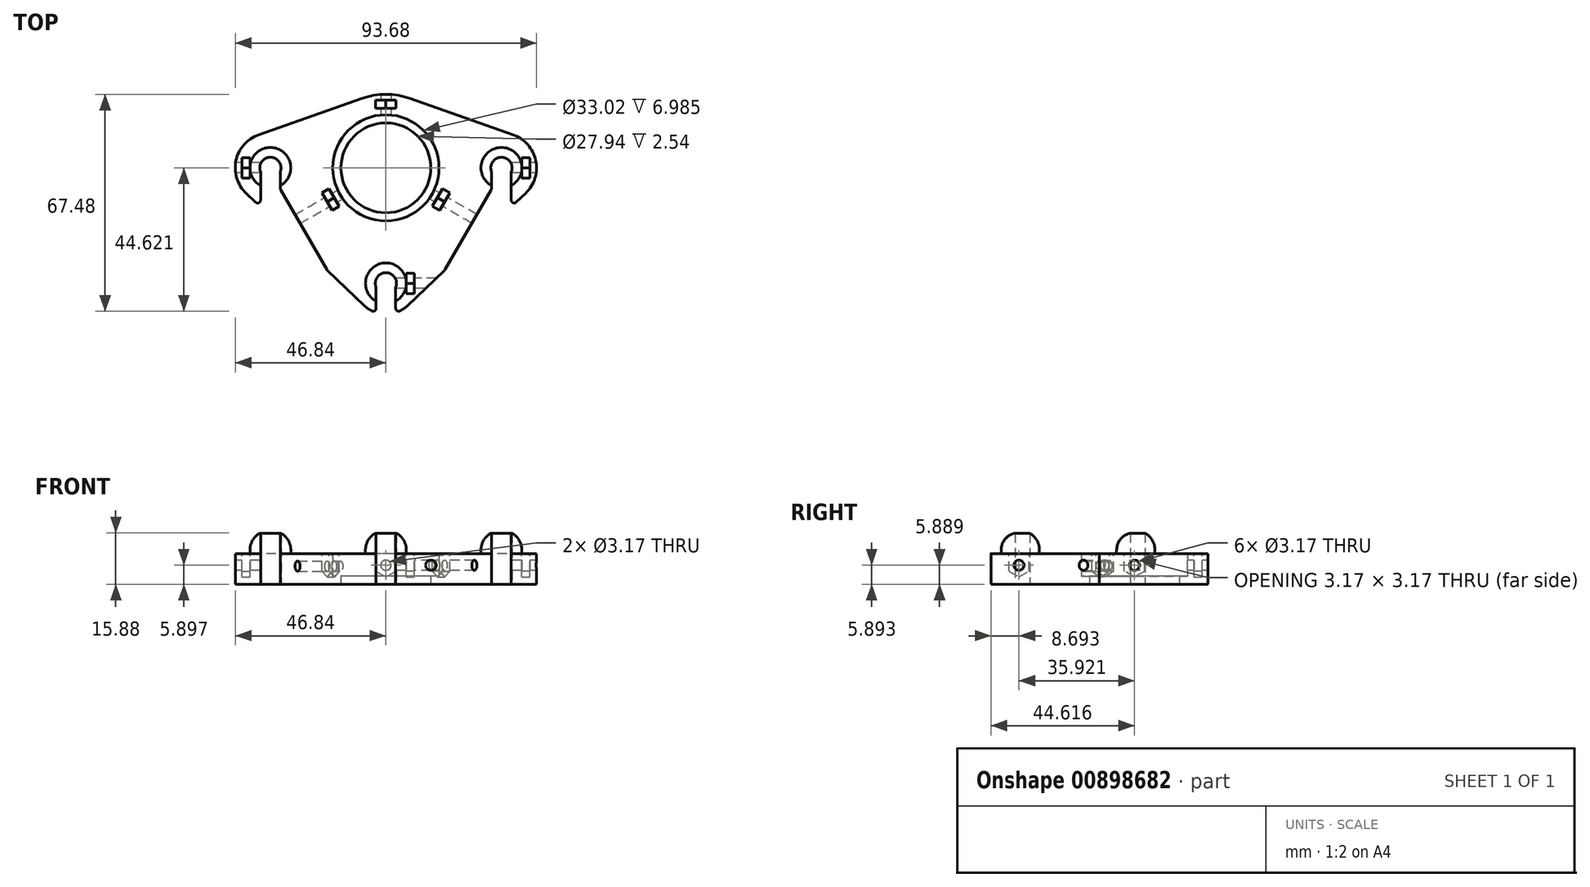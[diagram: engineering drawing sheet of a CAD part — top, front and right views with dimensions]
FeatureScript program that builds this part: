
annotation { "Feature Type Name" : "Feature", "Feature Type Description" : "" }
export const myFeature = defineFeature(function(context is Context, id is Id, definition is map)
    precondition{}
    {
        {
            var Q0;
            Q0=qCreatedBy(makeId("Top.planeOp"),FACE);
            var sketch = newSketch(context, id + "F0", { "sketchPlane" : qUnion([Q0])});
            skArc(sketch, "E0", {"start": v(3.05, -1.27) * mm, "mid": v(0, 3.3) * mm, "end": v(-3.05, -1.27) * mm});
            skArc(sketch, "E1", {"start": v(-32.87, 34.65) * mm, "mid": v(-35.92, 39.22) * mm, "end": v(-38.97, 34.65) * mm});
            skArc(sketch, "E2", {"start": v(38.97, 34.65) * mm, "mid": v(35.92, 39.22) * mm, "end": v(32.87, 34.65) * mm});
            skCircle(sketch, "E3", {"center": v(0, 35.92) * mm, "radius": 16.51 * mm});
            skArc(sketch, "E4.0", {"start": v(-39.55, 46.22) * mm, "mid": v(-46.6, 38.2) * mm, "end": v(-43.45, 28) * mm});
            skArc(sketch, "E5.0", {"start": v(7.6, 57.48) * mm, "mid": v(0, 58.78) * mm, "end": v(-7.6, 57.48) * mm});
            skArc(sketch, "E6.0", {"start": v(43.45, 28) * mm, "mid": v(46.6, 38.2) * mm, "end": v(39.55, 46.22) * mm});
            skArc(sketch, "E7.0", {"start": v(-6.65, -7) * mm, "mid": v(-5.57, -7.88) * mm, "end": v(-4.38, -8.6) * mm});
            skLineSegment(sketch, "E8", {"start": v(-39.55, 46.22) * mm, "end": v(-7.6, 57.48) * mm});
            skLineSegment(sketch, "E9", {"start": v(7.6, 57.48) * mm, "end": v(39.55, 46.22) * mm});
            skLineSegment(sketch, "E10", {"start": v(43.45, 28) * mm, "end": v(40.52, 25.22) * mm});
            skLineSegment(sketch, "E11", {"start": v(-6.65, -7) * mm, "end": v(-18.1, 3.9) * mm});
            skCircle(sketch, "E12", {"center": v(-35.92, 35.92) * mm, "radius": 3.05 * mm, "construction": true});
            skCircle(sketch, "E13", {"center": v(35.92, 35.92) * mm, "radius": 3.05 * mm, "construction": true});
            skCircle(sketch, "E14", {"center": v(0, 0) * mm, "radius": 3.05 * mm, "construction": true});
            skLineSegment(sketch, "E15", {"start": v(-32.87, 35.92) * mm, "end": v(-32.87, 29.77) * mm});
            skLineSegment(sketch, "E16", {"start": v(-38.97, 35.92) * mm, "end": v(-38.97, 25.88) * mm});
            skLineSegment(sketch, "E17", {"start": v(-3.05, 0) * mm, "end": v(-3.05, -7.79) * mm});
            skLineSegment(sketch, "E18", {"start": v(3.05, 0) * mm, "end": v(3.05, -7.79) * mm});
            skPoint(sketch, "E19", {"position": v(-3.05, -1.27) * mm});
            skPoint(sketch, "E20", {"position": v(3.05, -1.27) * mm});
            skArc(sketch, "E21.trimOffspring", {"start": v(4.38, -8.6) * mm, "mid": v(5.57, -7.88) * mm, "end": v(6.65, -7) * mm});
            skLineSegment(sketch, "E22.trimOffspring", {"start": v(-40.52, 25.22) * mm, "end": v(-43.45, 28) * mm});
            skPoint(sketch, "E23.visualSharp", {"position": v(-38.97, 23.75) * mm});
            skArc(sketch, "E23.filletArc", {"start": v(-40.52, 25.22) * mm, "mid": v(-39.52, 25.04) * mm, "end": v(-38.97, 25.88) * mm});
            skPoint(sketch, "E24.visualSharp", {"position": v(-3.05, -9.16) * mm});
            skArc(sketch, "E24.filletArc", {"start": v(-4.38, -8.6) * mm, "mid": v(-3.49, -8.57) * mm, "end": v(-3.05, -7.79) * mm});
            skPoint(sketch, "E25.visualSharp", {"position": v(3.05, -9.16) * mm});
            skArc(sketch, "E25.filletArc", {"start": v(3.05, -7.79) * mm, "mid": v(3.49, -8.57) * mm, "end": v(4.38, -8.6) * mm});
            skLineSegment(sketch, "E26", {"start": v(32.87, 35.92) * mm, "end": v(32.87, 29.77) * mm});
            skLineSegment(sketch, "E27", {"start": v(38.97, 35.92) * mm, "end": v(38.97, 25.88) * mm});
            skLineSegment(sketch, "E28.trimOffspring", {"start": v(18.1, 3.9) * mm, "end": v(6.65, -7) * mm});
            skPoint(sketch, "E29.visualSharp", {"position": v(38.97, 23.75) * mm});
            skCircle(sketch, "E30.0", {"center": v(0, 35.92) * mm, "radius": 13.97 * mm});
            skLineSegment(sketch, "E31", {"start": v(0, 35.92) * mm, "end": v(0, 52.43) * mm, "construction": true});
            skLineSegment(sketch, "E32", {"start": v(0, 35.92) * mm, "end": v(35.3, 15.54) * mm, "construction": true});
            skLineSegment(sketch, "E33", {"start": v(0, 35.92) * mm, "end": v(-35.36, 15.5) * mm, "construction": true});
            skArc(sketch, "E34.filletArc", {"start": v(38.97, 25.88) * mm, "mid": v(39.52, 25.04) * mm, "end": v(40.52, 25.22) * mm});
            skCircle(sketch, "E35.cCircle", {"center": v(0, 35.92) * mm, "radius": 16.51 * mm, "construction": true});
            skLineSegment(sketch, "E35.0", {"start": v(9.53, 52.43) * mm, "end": v(19.06, 35.92) * mm, "construction": true});
            skLineSegment(sketch, "E35.1", {"start": v(19.06, 35.92) * mm, "end": v(9.53, 19.41) * mm, "construction": true});
            skLineSegment(sketch, "E35.2", {"start": v(9.53, 19.41) * mm, "end": v(-9.53, 19.41) * mm, "construction": true});
            skLineSegment(sketch, "E35.3", {"start": v(-9.53, 19.41) * mm, "end": v(-19.06, 35.92) * mm, "construction": true});
            skLineSegment(sketch, "E35.4", {"start": v(-19.06, 35.92) * mm, "end": v(-9.53, 52.43) * mm, "construction": true});
            skLineSegment(sketch, "E35.5", {"start": v(-9.53, 52.43) * mm, "end": v(9.53, 52.43) * mm, "construction": true});
            skPoint(sketch, "E35.0.midPoint", {"position": v(14.3, 44.18) * mm});
            skLineSegment(sketch, "E36", {"start": v(-35.92, 35.92) * mm, "end": v(35.92, 35.92) * mm, "construction": true});
            skCircle(sketch, "E37.0", {"center": v(0, 35.92) * mm, "radius": 31.75 * mm, "construction": true});
            skLineSegment(sketch, "E38", {"start": v(-32.67, 29) * mm, "end": v(-18.37, 4.24) * mm});
            skLineSegment(sketch, "E39", {"start": v(32.67, 29) * mm, "end": v(18.37, 4.24) * mm});
            skPoint(sketch, "E40.visualSharp", {"position": v(-32.87, 29.36) * mm});
            skArc(sketch, "E40.filletArc", {"start": v(-32.87, 29.77) * mm, "mid": v(-32.82, 29.37) * mm, "end": v(-32.67, 29) * mm});
            skPoint(sketch, "E41.visualSharp", {"position": v(-18.26, 4.05) * mm});
            skArc(sketch, "E41.filletArc", {"start": v(-18.37, 4.24) * mm, "mid": v(-18.25, 4.06) * mm, "end": v(-18.1, 3.9) * mm});
            skPoint(sketch, "E42.visualSharp", {"position": v(18.26, 4.05) * mm});
            skArc(sketch, "E42.filletArc", {"start": v(18.1, 3.9) * mm, "mid": v(18.25, 4.06) * mm, "end": v(18.37, 4.24) * mm});
            skPoint(sketch, "E43.visualSharp", {"position": v(32.87, 29.36) * mm});
            skArc(sketch, "E43.filletArc", {"start": v(32.67, 29) * mm, "mid": v(32.82, 29.37) * mm, "end": v(32.87, 29.77) * mm});
            skSolve(sketch);
        }
        {
            var Q0;
            {var subQ5=sQuery(id+"F0.wireOp",EDGE,"E0");Q0=makeQuery(id+"F0.imprint","IMPRINT",FACE,{"disambiguationData":[TD([[makeQuery(id+"F0.imprint","IMPRINT",EDGE,{"derivedFrom":subQ5}),-1.0]])]});}
            extrude(context, id + "F1", {"entities" : qUnion([Q0]), "depth" : 9.52 * mm, "offsetDistance" : 25.4 * mm});
        }
        {
            var Q0;
            Q0=makeQuery(id+"F0.imprint","IMPRINT",FACE,{"disambiguationData":[TD([[makeQuery(id+"F0.imprint","IMPRINT",EDGE,{"derivedFrom":sQuery(id+"F0.wireOp",EDGE,"E3")}),1.0]])]});
            extrude(context, id + "F2", {"entities" : qUnion([Q0]), "operationType" : NewBodyOperationType.ADD, "depth" : 2.54 * mm, "hasOffset" : true, "offsetDistance" : 6.35 * mm});
        }
        {
            var Q0;
            Q0=makeQuery(id+"F1.opExtrude","CAP_FACE",FACE,{"disambiguationData":[OSD([sQuery(id+"F0.wireOp",EDGE,"E0"),sQuery(id+"F0.wireOp",EDGE,"E1"),sQuery(id+"F0.wireOp",EDGE,"E2"),sQuery(id+"F0.wireOp",EDGE,"E3"),sQuery(id+"F0.wireOp",EDGE,"E4.0"),sQuery(id+"F0.wireOp",EDGE,"E5.0"),sQuery(id+"F0.wireOp",EDGE,"E6.0"),sQuery(id+"F0.wireOp",EDGE,"E7.0"),sQuery(id+"F0.wireOp",EDGE,"E8"),sQuery(id+"F0.wireOp",EDGE,"E9"),sQuery(id+"F0.wireOp",EDGE,"E10"),sQuery(id+"F0.wireOp",EDGE,"E11"),sQuery(id+"F0.wireOp",EDGE,"E15"),sQuery(id+"F0.wireOp",EDGE,"E16"),sQuery(id+"F0.wireOp",EDGE,"E17"),sQuery(id+"F0.wireOp",EDGE,"E18"),sQuery(id+"F0.wireOp",EDGE,"E21.trimOffspring"),sQuery(id+"F0.wireOp",EDGE,"E22.trimOffspring"),sQuery(id+"F0.wireOp",EDGE,"E23.filletArc"),sQuery(id+"F0.wireOp",EDGE,"E24.filletArc"),sQuery(id+"F0.wireOp",EDGE,"E25.filletArc"),sQuery(id+"F0.wireOp",EDGE,"E26"),sQuery(id+"F0.wireOp",EDGE,"E27"),sQuery(id+"F0.wireOp",EDGE,"E28.trimOffspring"),sQuery(id+"F0.wireOp",EDGE,"3LgmcLzA-5pnU-fFz7-q1u9-bpeBtAsCO3An"),sQuery(id+"F0.wireOp",EDGE,"4eo9xTR6-c1Fu-en91-zOid-S4E7wj55DmDX"),sQuery(id+"F0.wireOp",EDGE,"E34.filletArc"),sQuery(id+"F0.wireOp",EDGE,"0de4be46-af92-408f-a28e-b5eb566cc358.filletArc"),sQuery(id+"F0.wireOp",EDGE,"cd97e584-8722-4711-bad1-4d169eb79cda.filletArc"),sQuery(id+"F0.wireOp",EDGE,"a80f9f6f-3806-41d0-9fd0-596e0330244b.filletArc"),sQuery(id+"F0.wireOp",EDGE,"743a1c7c-530f-41f0-bede-06812bb20fe3.filletArc")])],"isStart":false});
            var sketch = newSketch(context, id + "F3", { "sketchPlane" : qUnion([Q0])});
            skCircle(sketch, "E44", {"center": v(-35.92, 35.92) * mm, "radius": 6.35 * mm});
            skCircle(sketch, "E45", {"center": v(35.92, 35.92) * mm, "radius": 6.35 * mm});
            skCircle(sketch, "E46", {"center": v(0, 0) * mm, "radius": 6.35 * mm});
            skSolve(sketch);
        }
        {
            var Q0;
            Q0=makeQuery(id+"F1.opExtrude","CAP_FACE",FACE,{"disambiguationData":[OSD([sQuery(id+"F0.wireOp",EDGE,"E0"),sQuery(id+"F0.wireOp",EDGE,"E1"),sQuery(id+"F0.wireOp",EDGE,"E2"),sQuery(id+"F0.wireOp",EDGE,"E3"),sQuery(id+"F0.wireOp",EDGE,"E4.0"),sQuery(id+"F0.wireOp",EDGE,"E5.0"),sQuery(id+"F0.wireOp",EDGE,"E6.0"),sQuery(id+"F0.wireOp",EDGE,"E7.0"),sQuery(id+"F0.wireOp",EDGE,"E8"),sQuery(id+"F0.wireOp",EDGE,"E9"),sQuery(id+"F0.wireOp",EDGE,"E10"),sQuery(id+"F0.wireOp",EDGE,"E11"),sQuery(id+"F0.wireOp",EDGE,"E15"),sQuery(id+"F0.wireOp",EDGE,"E16"),sQuery(id+"F0.wireOp",EDGE,"E17"),sQuery(id+"F0.wireOp",EDGE,"E18"),sQuery(id+"F0.wireOp",EDGE,"E21.trimOffspring"),sQuery(id+"F0.wireOp",EDGE,"E22.trimOffspring"),sQuery(id+"F0.wireOp",EDGE,"E23.filletArc"),sQuery(id+"F0.wireOp",EDGE,"2f08ad09-a47d-42bd-8f0e-b7f58f6490e4.filletArc"),sQuery(id+"F0.wireOp",EDGE,"E24.filletArc"),sQuery(id+"F0.wireOp",EDGE,"E25.filletArc"),sQuery(id+"F0.wireOp",EDGE,"E26"),sQuery(id+"F0.wireOp",EDGE,"E27"),sQuery(id+"F0.wireOp",EDGE,"E28.trimOffspring"),sQuery(id+"F0.wireOp",EDGE,"bfc3d6b4-ed7b-404a-8939-94d15189dd00.filletArc"),sQuery(id+"F0.wireOp",EDGE,"E29.filletArc")])],"isStart":false});
            var sketch = newSketch(context, id + "F4", { "sketchPlane" : qUnion([Q0])});
            skLineSegment(sketch, "E47", {"start": v(-3.18, 54.46) * mm, "end": v(-3.18, 57) * mm});
            skLineSegment(sketch, "E48", {"start": v(-3.18, 57) * mm, "end": v(3.17, 57) * mm});
            skLineSegment(sketch, "E49", {"start": v(3.17, 57) * mm, "end": v(3.17, 54.46) * mm});
            skLineSegment(sketch, "E50", {"start": v(3.17, 54.46) * mm, "end": v(-3.18, 54.46) * mm});
            skLineSegment(sketch, "E51", {"start": v(0, 52.43) * mm, "end": v(0, 54.46) * mm});
            skLineSegment(sketch, "E52.1.0", {"start": v(-17.65, 29.4) * mm, "end": v(-14.47, 23.9) * mm});
            skLineSegment(sketch, "E52.1.1", {"start": v(-19.85, 28.13) * mm, "end": v(-17.65, 29.4) * mm});
            skLineSegment(sketch, "E52.1.2", {"start": v(-16.67, 22.63) * mm, "end": v(-19.85, 28.13) * mm});
            skLineSegment(sketch, "E52.1.3", {"start": v(-14.47, 23.9) * mm, "end": v(-16.67, 22.63) * mm});
            skLineSegment(sketch, "E52.2.0", {"start": v(14.47, 23.9) * mm, "end": v(17.65, 29.4) * mm});
            skLineSegment(sketch, "E52.2.1", {"start": v(16.67, 22.63) * mm, "end": v(14.47, 23.9) * mm});
            skLineSegment(sketch, "E52.2.2", {"start": v(19.85, 28.13) * mm, "end": v(16.67, 22.63) * mm});
            skLineSegment(sketch, "E52.2.3", {"start": v(17.65, 29.4) * mm, "end": v(19.85, 28.13) * mm});
            skPoint(sketch, "E52.center", {"position": v(0, 35.92) * mm});
            skCircle(sketch, "E53", {"center": v(-35.92, 35.92) * mm, "radius": 6.35 * mm});
            skCircle(sketch, "E54", {"center": v(35.92, 35.92) * mm, "radius": 6.35 * mm});
            skCircle(sketch, "E55", {"center": v(0, 0) * mm, "radius": 6.35 * mm});
            skLineSegment(sketch, "E56", {"start": v(-42.27, 39.1) * mm, "end": v(-42.27, 32.75) * mm});
            skLineSegment(sketch, "E57", {"start": v(-42.27, 32.75) * mm, "end": v(-44.81, 32.75) * mm});
            skLineSegment(sketch, "E58", {"start": v(-44.81, 32.75) * mm, "end": v(-44.81, 39.1) * mm});
            skLineSegment(sketch, "E59", {"start": v(-44.81, 39.1) * mm, "end": v(-42.27, 39.1) * mm});
            skLineSegment(sketch, "E60", {"start": v(-35.92, 35.92) * mm, "end": v(-42.27, 35.92) * mm, "construction": true});
            skLineSegment(sketch, "E61", {"start": v(42.27, 32.75) * mm, "end": v(42.27, 39.1) * mm});
            skLineSegment(sketch, "E62", {"start": v(42.27, 39.1) * mm, "end": v(44.81, 39.1) * mm});
            skLineSegment(sketch, "E63", {"start": v(44.81, 39.1) * mm, "end": v(44.81, 32.75) * mm});
            skLineSegment(sketch, "E64", {"start": v(44.81, 32.75) * mm, "end": v(42.27, 32.75) * mm});
            skLineSegment(sketch, "E65", {"start": v(35.92, 35.92) * mm, "end": v(42.27, 35.92) * mm, "construction": true});
            skLineSegment(sketch, "E66", {"start": v(8.9, 3.18) * mm, "end": v(8.9, -3.18) * mm});
            skLineSegment(sketch, "E67", {"start": v(8.9, -3.18) * mm, "end": v(6.35, -3.18) * mm});
            skLineSegment(sketch, "E68", {"start": v(6.35, -3.18) * mm, "end": v(6.35, 3.18) * mm});
            skLineSegment(sketch, "E69", {"start": v(6.35, 3.17) * mm, "end": v(8.9, 3.17) * mm});
            skLineSegment(sketch, "E70", {"start": v(8.9, 0) * mm, "end": v(0, 0) * mm, "construction": true});
            skSolve(sketch);
        }
        {
            var Q0;
            Q0=makeQuery(id+"F4.imprint","IMPRINT",FACE,{"disambiguationData":[TD([[makeQuery(id+"F4.imprint","IMPRINT",EDGE,{"derivedFrom":sQuery(id+"F4.wireOp",EDGE,"E52.2.0")}),-1.0]])]});
            var Q1;
            {var subQ3=sQuery(id+"F4.wireOp",EDGE,"E47");Q1=makeQuery(id+"F4.imprint","IMPRINT",FACE,{"disambiguationData":[TD([[makeQuery(id+"F4.imprint","IMPRINT",EDGE,{"derivedFrom":subQ3}),-1.0]])]});}
            var Q2;
            Q2=makeQuery(id+"F4.imprint","IMPRINT",FACE,{"disambiguationData":[TD([[makeQuery(id+"F4.imprint","IMPRINT",EDGE,{"derivedFrom":sQuery(id+"F4.wireOp",EDGE,"E52.1.0")}),-1.0]])]});
            var Q3;
            {var subQ0=sQuery(id+"F4.wireOp",EDGE,"E57");Q3=makeQuery(id+"F4.imprint","IMPRINT",FACE,{"disambiguationData":[TD([[makeQuery(id+"F4.imprint","IMPRINT",EDGE,{"derivedFrom":subQ0}),-1.0]])]});}
            var Q4;
            {var subQ0=sQuery(id+"F4.wireOp",EDGE,"E62");Q4=makeQuery(id+"F4.imprint","IMPRINT",FACE,{"disambiguationData":[TD([[makeQuery(id+"F4.imprint","IMPRINT",EDGE,{"derivedFrom":subQ0}),-1.0]])]});}
            var Q5;
            Q5=makeQuery(id+"F4.imprint","IMPRINT",FACE,{"disambiguationData":[TD([[makeQuery(id+"F4.imprint","IMPRINT",EDGE,{"derivedFrom":sQuery(id+"F4.wireOp",EDGE,"E66")}),-1.0]])]});
            extrude(context, id + "F5", {"entities" : qUnion([Q0, Q1, Q2, Q3, Q4, Q5]), "operationType" : NewBodyOperationType.REMOVE, "oppositeDirection" : true, "depth" : 8.64 * mm, "offsetDistance" : 25.4 * mm});
        }
        {
            var Q0;
            Q0=makeQuery(id+"F5.boolean.opBoolean","COPY",EDGE,{"derivedFrom":makeQuery(id+"F5.opExtrude","CAP_EDGE",EDGE,{"disambiguationData":[OSD([sQuery(id+"F4.wireOp",EDGE,"E52.1.1")])],"isStart":false})});
            var Q1;
            Q1=makeQuery(id+"F5.boolean.opBoolean","COPY",EDGE,{"derivedFrom":makeQuery(id+"F5.opExtrude","CAP_EDGE",EDGE,{"disambiguationData":[OSD([sQuery(id+"F4.wireOp",EDGE,"E52.1.3")])],"isStart":false})});
            var Q2;
            Q2=makeQuery(id+"F5.boolean.opBoolean","COPY",EDGE,{"derivedFrom":makeQuery(id+"F5.opExtrude","CAP_EDGE",EDGE,{"disambiguationData":[OSD([sQuery(id+"F4.wireOp",EDGE,"E47")])],"isStart":false})});
            var Q3;
            Q3=makeQuery(id+"F5.boolean.opBoolean","COPY",EDGE,{"derivedFrom":makeQuery(id+"F5.opExtrude","CAP_EDGE",EDGE,{"disambiguationData":[OSD([sQuery(id+"F4.wireOp",EDGE,"E49")])],"isStart":false})});
            var Q4;
            Q4=makeQuery(id+"F5.boolean.opBoolean","COPY",EDGE,{"derivedFrom":makeQuery(id+"F5.opExtrude","CAP_EDGE",EDGE,{"disambiguationData":[OSD([sQuery(id+"F4.wireOp",EDGE,"E52.2.3")])],"isStart":false})});
            var Q5;
            Q5=makeQuery(id+"F5.boolean.opBoolean","COPY",EDGE,{"derivedFrom":makeQuery(id+"F5.opExtrude","CAP_EDGE",EDGE,{"disambiguationData":[OSD([sQuery(id+"F4.wireOp",EDGE,"E52.2.1")])],"isStart":false})});
            var Q6;
            Q6=makeQuery(id+"F5.boolean.opBoolean","COPY",EDGE,{"derivedFrom":makeQuery(id+"F5.opExtrude","CAP_EDGE",EDGE,{"disambiguationData":[OSD([sQuery(id+"F4.wireOp",EDGE,"E59")])],"isStart":false})});
            var Q7;
            Q7=makeQuery(id+"F5.boolean.opBoolean","COPY",EDGE,{"derivedFrom":makeQuery(id+"F5.opExtrude","CAP_EDGE",EDGE,{"disambiguationData":[OSD([sQuery(id+"F4.wireOp",EDGE,"E57")])],"isStart":false})});
            var Q8;
            Q8=makeQuery(id+"F5.boolean.opBoolean","COPY",EDGE,{"derivedFrom":makeQuery(id+"F5.opExtrude","CAP_EDGE",EDGE,{"disambiguationData":[OSD([sQuery(id+"F4.wireOp",EDGE,"E69")])],"isStart":false})});
            var Q9;
            Q9=makeQuery(id+"F5.boolean.opBoolean","COPY",EDGE,{"derivedFrom":makeQuery(id+"F5.opExtrude","CAP_EDGE",EDGE,{"disambiguationData":[OSD([sQuery(id+"F4.wireOp",EDGE,"E67")])],"isStart":false})});
            var Q10;
            Q10=makeQuery(id+"F5.boolean.opBoolean","COPY",EDGE,{"derivedFrom":makeQuery(id+"F5.opExtrude","CAP_EDGE",EDGE,{"disambiguationData":[OSD([sQuery(id+"F4.wireOp",EDGE,"E62")])],"isStart":false})});
            var Q11;
            Q11=makeQuery(id+"F5.boolean.opBoolean","COPY",EDGE,{"derivedFrom":makeQuery(id+"F5.opExtrude","CAP_EDGE",EDGE,{"disambiguationData":[OSD([sQuery(id+"F4.wireOp",EDGE,"E64")])],"isStart":false})});
            chamfer(context, id + "F6", {"entities" : qUnion([Q0, Q1, Q2, Q3, Q4, Q5, Q6, Q7, Q8, Q9, Q10, Q11]), "chamferType" : ChamferType.OFFSET_ANGLE, "width" : 3.17 * mm, "oppositeDirection" : false, "angle" : 60 * degree, "tangentPropagation" : true});
        }
        {
            var Q0;
            Q0=makeQuery(id+"F5.boolean.opBoolean","COPY",FACE,{"derivedFrom":makeQuery(id+"F5.opExtrude","SWEPT_FACE",FACE,{"disambiguationData":[OSD([sQuery(id+"F4.wireOp",EDGE,"E48")])]})});
            var sketch = newSketch(context, id + "F7", { "sketchPlane" : qUnion([Q0])});
            skLineSegment(sketch, "E71", {"start": v(3.18, 4.06) * mm, "end": v(0, 2.23) * mm});
            skLineSegment(sketch, "E72", {"start": v(0, 2.23) * mm, "end": v(-3.17, 4.06) * mm});
            skLineSegment(sketch, "E73", {"start": v(-3.17, 4.06) * mm, "end": v(-3.17, 7.73) * mm});
            skLineSegment(sketch, "E74", {"start": v(3.18, 7.73) * mm, "end": v(3.18, 4.06) * mm});
            skLineSegment(sketch, "E75", {"start": v(3.18, 7.73) * mm, "end": v(0, 9.56) * mm});
            skPoint(sketch, "E75.endSnap0", {"position": v(0, 9.53) * mm});
            skLineSegment(sketch, "E76", {"start": v(0, 9.56) * mm, "end": v(-3.17, 7.73) * mm});
            skLineSegment(sketch, "E77", {"start": v(0, 2.23) * mm, "end": v(0, 5.9) * mm, "construction": true});
            skLineSegment(sketch, "E78", {"start": v(0, 5.9) * mm, "end": v(-3.17, 4.06) * mm, "construction": true});
            skLineSegment(sketch, "E79", {"start": v(0, 5.9) * mm, "end": v(3.18, 7.73) * mm, "construction": true});
            skLineSegment(sketch, "E80", {"start": v(0, 5.9) * mm, "end": v(0, 9.56) * mm, "construction": true});
            skCircle(sketch, "E81", {"center": v(0, 5.9) * mm, "radius": 1.59 * mm});
            skSolve(sketch);
        }
        {
            var Q0;
            Q0=makeQuery(id+"F5.boolean.opBoolean","COPY",FACE,{"derivedFrom":makeQuery(id+"F5.opExtrude","SWEPT_FACE",FACE,{"disambiguationData":[OSD([sQuery(id+"F4.wireOp",EDGE,"E52.1.2")])]})});
            var sketch = newSketch(context, id + "F8", { "sketchPlane" : qUnion([Q0])});
            skLineSegment(sketch, "E82", {"start": v(34.2, 3.78) * mm, "end": v(31.03, 1.94) * mm});
            skLineSegment(sketch, "E83", {"start": v(31.03, 1.94) * mm, "end": v(27.86, 3.78) * mm});
            skLineSegment(sketch, "E84", {"start": v(27.86, 3.78) * mm, "end": v(27.86, 7.44) * mm});
            skLineSegment(sketch, "E85", {"start": v(34.2, 7.44) * mm, "end": v(34.2, 3.78) * mm});
            skLineSegment(sketch, "E86", {"start": v(34.2, 7.44) * mm, "end": v(31.03, 9.26) * mm});
            skLineSegment(sketch, "E87", {"start": v(31.03, 9.26) * mm, "end": v(27.86, 7.44) * mm});
            skCircle(sketch, "E88", {"center": v(31.03, 5.6) * mm, "radius": 1.59 * mm});
            skSolve(sketch);
        }
        {
            var Q0;
            Q0=makeQuery(id+"F5.boolean.opBoolean","COPY",FACE,{"derivedFrom":makeQuery(id+"F5.opExtrude","SWEPT_FACE",FACE,{"disambiguationData":[OSD([sQuery(id+"F4.wireOp",EDGE,"E52.2.2")])]})});
            var sketch = newSketch(context, id + "F9", { "sketchPlane" : qUnion([Q0])});
            skLineSegment(sketch, "E89", {"start": v(-27.95, 4.06) * mm, "end": v(-31.12, 2.24) * mm});
            skLineSegment(sketch, "E90", {"start": v(-31.12, 2.24) * mm, "end": v(-34.28, 4.06) * mm});
            skLineSegment(sketch, "E91", {"start": v(-34.28, 4.06) * mm, "end": v(-34.28, 7.72) * mm});
            skLineSegment(sketch, "E92", {"start": v(-27.95, 7.72) * mm, "end": v(-27.95, 4.06) * mm});
            skLineSegment(sketch, "E93", {"start": v(-27.95, 7.72) * mm, "end": v(-31.12, 9.55) * mm});
            skLineSegment(sketch, "E94", {"start": v(-31.12, 9.55) * mm, "end": v(-34.28, 7.72) * mm});
            skCircle(sketch, "E95", {"center": v(-31.12, 5.9) * mm, "radius": 1.59 * mm});
            skLineSegment(sketch, "E96", {"start": v(-31.12, 2.24) * mm, "end": v(-31.12, 5.9) * mm, "construction": true});
            skLineSegment(sketch, "E97", {"start": v(-31.12, 5.9) * mm, "end": v(-34.28, 4.06) * mm, "construction": true});
            skLineSegment(sketch, "E98", {"start": v(-31.12, 9.55) * mm, "end": v(-31.12, 5.9) * mm, "construction": true});
            skLineSegment(sketch, "E99", {"start": v(-27.95, 7.72) * mm, "end": v(-31.12, 5.9) * mm, "construction": true});
            skSolve(sketch);
        }
        {
            var Q0;
            Q0=makeQuery(id+"F7.imprint","IMPRINT",FACE,{"disambiguationData":[TD([[makeQuery(id+"F7.imprint","IMPRINT",EDGE,{"derivedFrom":sQuery(id+"F7.wireOp",EDGE,"E81")}),1.0]])]});
            extrude(context, id + "F10", {"entities" : qUnion([Q0]), "operationType" : NewBodyOperationType.REMOVE, "oppositeDirection" : true, "depth" : 10.16 * mm, "offsetDistance" : 25.4 * mm, "symmetric" : true});
        }
        {
            var Q0;
            Q0=makeQuery(id+"F8.imprint","IMPRINT",FACE,{"disambiguationData":[TD([[makeQuery(id+"F8.imprint","IMPRINT",EDGE,{"derivedFrom":sQuery(id+"F8.wireOp",EDGE,"E88")}),1.0]])]});
            var Q1;
            Q1=sQuery(id+"F8.wireOp",EDGE,"E88");
            extrude(context, id + "F11", {"entities" : qUnion([Q0]), "operationType" : NewBodyOperationType.REMOVE, "surfaceEntities" : qUnion([Q1]), "oppositeDirection" : true, "depth" : 40.64 * mm, "offsetDistance" : 25.4 * mm, "symmetric" : true});
        }
        {
            var Q0;
            Q0=makeQuery(id+"F9.imprint","IMPRINT",FACE,{"disambiguationData":[TD([[makeQuery(id+"F9.imprint","IMPRINT",EDGE,{"derivedFrom":sQuery(id+"F9.wireOp",EDGE,"E95")}),1.0]])]});
            var Q1;
            Q1=sQuery(id+"F9.wireOp",EDGE,"E95");
            extrude(context, id + "F12", {"entities" : qUnion([Q0]), "operationType" : NewBodyOperationType.REMOVE, "surfaceEntities" : qUnion([Q1]), "oppositeDirection" : true, "depth" : 40.64 * mm, "offsetDistance" : 25.4 * mm, "symmetric" : true});
        }
        {
            var Q0;
            {var subQ5=makeQuery(id+"F1.opExtrude","CAP_EDGE",EDGE,{"disambiguationData":[OSD([sQuery(id+"F0.wireOp",EDGE,"E1")])],"isStart":false});Q0=makeQuery(id+"F3.imprint","IMPRINT",FACE,{"disambiguationData":[TD([[makeQuery(id+"F3.imprint","IMPRINT",EDGE,{"derivedFrom":subQ5}),-1.0]])]});}
            var Q1;
            {var subQ5=makeQuery(id+"F1.opExtrude","CAP_EDGE",EDGE,{"disambiguationData":[OSD([sQuery(id+"F0.wireOp",EDGE,"E2")])],"isStart":false});Q1=makeQuery(id+"F3.imprint","IMPRINT",FACE,{"disambiguationData":[TD([[makeQuery(id+"F3.imprint","IMPRINT",EDGE,{"derivedFrom":subQ5}),-1.0]])]});}
            var Q2;
            {var subQ5=makeQuery(id+"F1.opExtrude","CAP_EDGE",EDGE,{"disambiguationData":[OSD([sQuery(id+"F0.wireOp",EDGE,"E0")])],"isStart":false});Q2=makeQuery(id+"F3.imprint","IMPRINT",FACE,{"disambiguationData":[TD([[makeQuery(id+"F3.imprint","IMPRINT",EDGE,{"derivedFrom":subQ5}),-1.0]])]});}
            extrude(context, id + "F13", {"entities" : qUnion([Q0, Q1, Q2]), "operationType" : NewBodyOperationType.ADD, "depth" : 6.35 * mm, "offsetDistance" : 25.4 * mm});
        }
        {
            var Q0;
            Q0=makeQuery(id+"F13.opExtrude","CAP_EDGE",EDGE,{"disambiguationData":[OSD([sQuery(id+"F3.wireOp",EDGE,"E44")])],"isStart":false});
            var Q1;
            Q1=makeQuery(id+"F13.opExtrude","CAP_EDGE",EDGE,{"disambiguationData":[OSD([sQuery(id+"F3.wireOp",EDGE,"E45")])],"isStart":false});
            var Q2;
            Q2=makeQuery(id+"F13.opExtrude","CAP_EDGE",EDGE,{"disambiguationData":[OSD([sQuery(id+"F3.wireOp",EDGE,"E46")])],"isStart":false});
            fillet(context, id + "F14", {"entities" : qUnion([Q0, Q1, Q2]), "radius" : 6.1 * mm, "tangentPropagation" : true, "allowEdgeOverflow" : false});
        }
        {
            var Q0;
            Q0=makeQuery(id+"F5.boolean.opBoolean","COPY",FACE,{"derivedFrom":makeQuery(id+"F5.opExtrude","SWEPT_FACE",FACE,{"disambiguationData":[OSD([sQuery(id+"F4.wireOp",EDGE,"E58")])]})});
            var sketch = newSketch(context, id + "F15", { "sketchPlane" : qUnion([Q0])});
            skLineSegment(sketch, "E100", {"start": v(39.08, 4.06) * mm, "end": v(35.91, 2.24) * mm});
            skLineSegment(sketch, "E101", {"start": v(35.91, 2.24) * mm, "end": v(32.75, 4.06) * mm});
            skLineSegment(sketch, "E102", {"start": v(32.75, 4.06) * mm, "end": v(32.75, 7.72) * mm});
            skLineSegment(sketch, "E103", {"start": v(39.08, 7.72) * mm, "end": v(39.08, 4.06) * mm});
            skLineSegment(sketch, "E104", {"start": v(39.08, 7.72) * mm, "end": v(35.91, 9.55) * mm});
            skLineSegment(sketch, "E105", {"start": v(35.91, 9.55) * mm, "end": v(32.75, 7.72) * mm});
            skLineSegment(sketch, "E106", {"start": v(35.91, 2.24) * mm, "end": v(35.91, 5.9) * mm, "construction": true});
            skLineSegment(sketch, "E107", {"start": v(35.91, 5.9) * mm, "end": v(32.75, 4.06) * mm, "construction": true});
            skLineSegment(sketch, "E108", {"start": v(35.91, 5.9) * mm, "end": v(39.08, 7.72) * mm, "construction": true});
            skLineSegment(sketch, "E109", {"start": v(35.91, 5.9) * mm, "end": v(35.91, 9.55) * mm, "construction": true});
            skCircle(sketch, "E110", {"center": v(35.91, 5.9) * mm, "radius": 1.59 * mm});
            skSolve(sketch);
        }
        {
            var Q0;
            Q0=makeQuery(id+"F5.boolean.opBoolean","COPY",FACE,{"derivedFrom":makeQuery(id+"F5.opExtrude","SWEPT_FACE",FACE,{"disambiguationData":[OSD([sQuery(id+"F4.wireOp",EDGE,"E66")])]})});
            var sketch = newSketch(context, id + "F16", { "sketchPlane" : qUnion([Q0])});
            skLineSegment(sketch, "E111", {"start": v(3.18, 4.06) * mm, "end": v(0, 2.24) * mm});
            skLineSegment(sketch, "E112", {"start": v(0, 2.24) * mm, "end": v(-3.16, 4.06) * mm});
            skLineSegment(sketch, "E113", {"start": v(-3.16, 4.06) * mm, "end": v(-3.16, 7.72) * mm});
            skLineSegment(sketch, "E114", {"start": v(3.18, 7.72) * mm, "end": v(3.18, 4.06) * mm});
            skLineSegment(sketch, "E115", {"start": v(3.18, 7.72) * mm, "end": v(0, 9.55) * mm});
            skLineSegment(sketch, "E116", {"start": v(0, 9.55) * mm, "end": v(-3.16, 7.72) * mm});
            skLineSegment(sketch, "E117", {"start": v(0, 2.24) * mm, "end": v(0, 5.9) * mm, "construction": true});
            skLineSegment(sketch, "E118", {"start": v(0, 5.9) * mm, "end": v(-3.16, 4.06) * mm, "construction": true});
            skLineSegment(sketch, "E119", {"start": v(0, 5.9) * mm, "end": v(3.18, 7.72) * mm, "construction": true});
            skLineSegment(sketch, "E120", {"start": v(0, 5.9) * mm, "end": v(0, 9.55) * mm, "construction": true});
            skCircle(sketch, "E121", {"center": v(0, 5.9) * mm, "radius": 1.59 * mm});
            skSolve(sketch);
        }
        {
            var Q0;
            Q0=makeQuery(id+"F5.boolean.opBoolean","COPY",FACE,{"derivedFrom":makeQuery(id+"F5.opExtrude","SWEPT_FACE",FACE,{"disambiguationData":[OSD([sQuery(id+"F4.wireOp",EDGE,"E63")])]})});
            var sketch = newSketch(context, id + "F17", { "sketchPlane" : qUnion([Q0])});
            skLineSegment(sketch, "E122", {"start": v(-32.75, 4.06) * mm, "end": v(-35.91, 2.24) * mm});
            skLineSegment(sketch, "E123", {"start": v(-35.91, 2.24) * mm, "end": v(-39.08, 4.06) * mm});
            skLineSegment(sketch, "E124", {"start": v(-39.08, 4.06) * mm, "end": v(-39.08, 7.72) * mm});
            skLineSegment(sketch, "E125", {"start": v(-32.75, 7.72) * mm, "end": v(-32.75, 4.06) * mm});
            skLineSegment(sketch, "E126", {"start": v(-32.75, 7.72) * mm, "end": v(-35.91, 9.55) * mm});
            skLineSegment(sketch, "E127", {"start": v(-35.91, 9.55) * mm, "end": v(-39.08, 7.72) * mm});
            skLineSegment(sketch, "E128", {"start": v(-35.91, 2.24) * mm, "end": v(-35.91, 5.9) * mm, "construction": true});
            skLineSegment(sketch, "E129", {"start": v(-35.91, 5.9) * mm, "end": v(-39.08, 4.06) * mm, "construction": true});
            skLineSegment(sketch, "E130", {"start": v(-35.91, 5.9) * mm, "end": v(-32.75, 7.72) * mm, "construction": true});
            skLineSegment(sketch, "E131", {"start": v(-35.91, 5.9) * mm, "end": v(-35.91, 9.55) * mm, "construction": true});
            skCircle(sketch, "E132", {"center": v(-35.91, 5.9) * mm, "radius": 1.59 * mm});
            skSolve(sketch);
        }
        {
            var Q0;
            Q0=makeQuery(id+"F17.imprint","IMPRINT",FACE,{"disambiguationData":[TD([[makeQuery(id+"F17.imprint","IMPRINT",EDGE,{"derivedFrom":sQuery(id+"F17.wireOp",EDGE,"E132")}),1.0]])]});
            var Q1;
            Q1=sQuery(id+"F17.wireOp",EDGE,"E132");
            extrude(context, id + "F18", {"entities" : qUnion([Q0]), "operationType" : NewBodyOperationType.REMOVE, "surfaceEntities" : qUnion([Q1]), "oppositeDirection" : true, "depth" : 12.7 * mm, "offsetDistance" : 25.4 * mm, "symmetric" : true});
        }
        {
            var Q0;
            Q0=makeQuery(id+"F15.imprint","IMPRINT",FACE,{"disambiguationData":[TD([[makeQuery(id+"F15.imprint","IMPRINT",EDGE,{"derivedFrom":sQuery(id+"F15.wireOp",EDGE,"E110")}),1.0]])]});
            extrude(context, id + "F19", {"entities" : qUnion([Q0]), "operationType" : NewBodyOperationType.REMOVE, "depth" : 12.7 * mm, "offsetDistance" : 25.4 * mm, "symmetric" : true});
        }
        {
            var Q0;
            Q0=makeQuery(id+"F16.imprint","IMPRINT",FACE,{"disambiguationData":[TD([[makeQuery(id+"F16.imprint","IMPRINT",EDGE,{"derivedFrom":sQuery(id+"F16.wireOp",EDGE,"E121")}),1.0]])]});
            extrude(context, id + "F20", {"entities" : qUnion([Q0]), "operationType" : NewBodyOperationType.REMOVE, "oppositeDirection" : true, "depth" : 15.24 * mm, "offsetDistance" : 25.4 * mm, "symmetric" : true});
        }
    });
